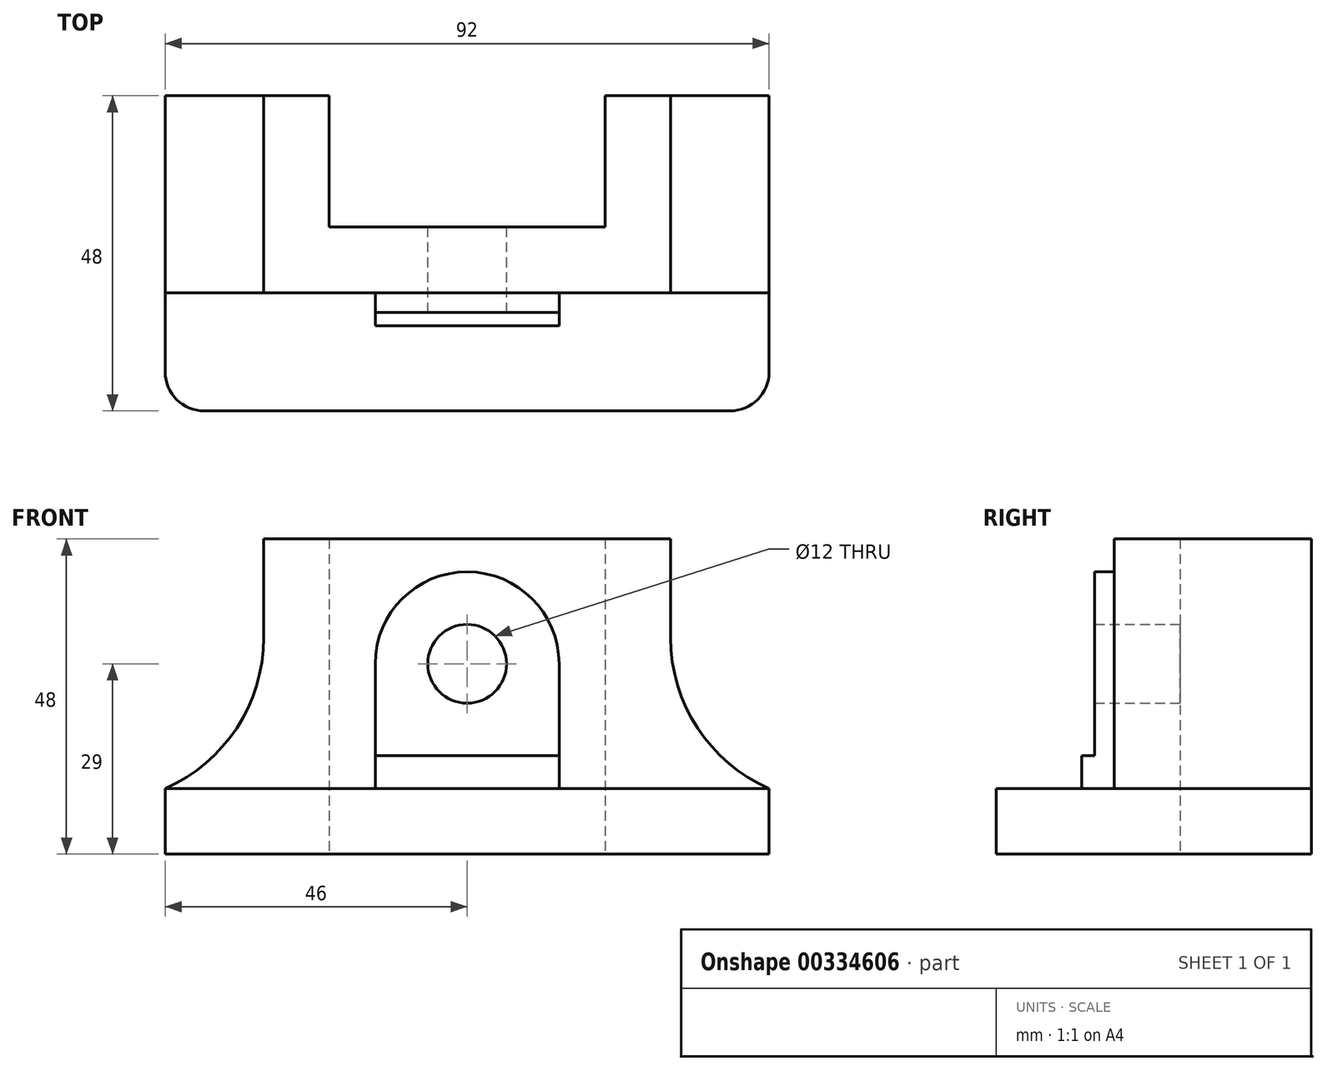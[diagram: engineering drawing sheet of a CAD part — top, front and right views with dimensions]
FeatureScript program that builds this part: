
annotation { "Feature Type Name" : "Feature", "Feature Type Description" : "" }
export const myFeature = defineFeature(function(context is Context, id is Id, definition is map)
    precondition{}
    {
        {
            var Q0;
            Q0=qCreatedBy(makeId("Top.planeOp"),FACE);
            var sketch = newSketch(context, id + "F0", { "sketchPlane" : qUnion([Q0])});
            skPoint(sketch, "E0.middle", {"position": v(0, 0) * mm});
            skLineSegment(sketch, "E1", {"start": v(0, 11.63) * mm, "end": v(-21, 11.63) * mm});
            skLineSegment(sketch, "E2", {"start": v(-21, 11.63) * mm, "end": v(-21, 31.63) * mm});
            skLineSegment(sketch, "E3", {"start": v(-21, 31.63) * mm, "end": v(-31, 31.63) * mm});
            skLineSegment(sketch, "E4", {"start": v(-31, 31.63) * mm, "end": v(-31, 1.63) * mm});
            skLineSegment(sketch, "E5", {"start": v(-31, 1.63) * mm, "end": v(0, 1.63) * mm});
            skLineSegment(sketch, "E6.MirrorCS", {"start": v(31, 31.63) * mm, "end": v(31, 1.63) * mm});
            skLineSegment(sketch, "E7.MirrorCS", {"start": v(31, 1.63) * mm, "end": v(0, 1.63) * mm});
            skLineSegment(sketch, "E8.MirrorCS", {"start": v(0, 11.63) * mm, "end": v(21, 11.63) * mm});
            skLineSegment(sketch, "E9.MirrorCS", {"start": v(21, 11.63) * mm, "end": v(21, 31.63) * mm});
            skLineSegment(sketch, "E10.MirrorCS", {"start": v(21, 31.63) * mm, "end": v(31, 31.63) * mm});
            skLineSegment(sketch, "E11", {"start": v(-46, 31.63) * mm, "end": v(-46, -16.37) * mm});
            skLineSegment(sketch, "E12", {"start": v(-46, -16.37) * mm, "end": v(0, -16.37) * mm});
            skLineSegment(sketch, "E13", {"start": v(-31, 31.63) * mm, "end": v(-46, 31.63) * mm});
            skLineSegment(sketch, "E14.MirrorCS", {"start": v(46, -16.37) * mm, "end": v(0, -16.37) * mm});
            skLineSegment(sketch, "E15.MirrorCS", {"start": v(31, 31.63) * mm, "end": v(46, 31.63) * mm});
            skLineSegment(sketch, "E16.MirrorCS", {"start": v(46, 31.63) * mm, "end": v(46, -16.37) * mm});
            skSolve(sketch);
        }
        {
            var Q0;
            Q0=makeQuery(id+"F0.imprint","IMPRINT",FACE,{"disambiguationData":[TD([[makeQuery(id+"F0.imprint","IMPRINT",EDGE,{"derivedFrom":sQuery(id+"F0.wireOp",EDGE,"E1")}),1.0]])]});
            extrude(context, id + "F1", {"entities" : qUnion([Q0]), "depth" : 48 * mm});
        }
        {
            var Q0;
            Q0 = qSketchRegion(id + "F0", true);
            extrude(context, id + "F2", {"entities" : qUnion([Q0]), "operationType" : NewBodyOperationType.ADD, "depth" : 10 * mm});
        }
        {
            var Q0;
            Q0=makeQuery(id+"F2.opExtrude","SWEPT_EDGE",EDGE,{"disambiguationData":[OSD([sQuery(id+"F0.wireOp",EDGE,"E11"),sQuery(id+"F0.wireOp",EDGE,"E12")])]});
            var Q1;
            Q1=makeQuery(id+"F2.opExtrude","SWEPT_EDGE",EDGE,{"disambiguationData":[OSD([sQuery(id+"F0.wireOp",EDGE,"E14.MirrorCS"),sQuery(id+"F0.wireOp",EDGE,"E16.MirrorCS")])]});
            fillet(context, id + "F3", {"entities" : qUnion([Q0, Q1]), "radius" : 6 * mm, "tangentPropagation" : true, "allowEdgeOverflow" : false});
        }
        {
            var Q0;
            Q0=makeQuery(id+"F2.boolean.opBoolean","INTERSECT",EDGE,{"derivedFrom":[makeQuery(id+"F1.opExtrude","SWEPT_FACE",FACE,{"disambiguationData":[OSD([sQuery(id+"F0.wireOp",EDGE,"E4")])]}),makeQuery(id+"F2.opExtrude","CAP_FACE",FACE,{"disambiguationData":[OSD([sQuery(id+"F0.wireOp",EDGE,"E1"),sQuery(id+"F0.wireOp",EDGE,"E2"),sQuery(id+"F0.wireOp",EDGE,"E3"),sQuery(id+"F0.wireOp",EDGE,"E8.MirrorCS"),sQuery(id+"F0.wireOp",EDGE,"E9.MirrorCS"),sQuery(id+"F0.wireOp",EDGE,"E10.MirrorCS"),sQuery(id+"F0.wireOp",EDGE,"E11"),sQuery(id+"F0.wireOp",EDGE,"E12"),sQuery(id+"F0.wireOp",EDGE,"E13"),sQuery(id+"F0.wireOp",EDGE,"E14.MirrorCS"),sQuery(id+"F0.wireOp",EDGE,"E15.MirrorCS"),sQuery(id+"F0.wireOp",EDGE,"E16.MirrorCS")])],"isStart":false})]});
            fillet(context, id + "F4", {"entities" : qUnion([Q0]), "radius" : 25 * mm, "tangentPropagation" : true, "allowEdgeOverflow" : false});
        }
        {
            var Q0;
            Q0=makeQuery(id+"F2.boolean.opBoolean","INTERSECT",EDGE,{"derivedFrom":[makeQuery(id+"F1.opExtrude","SWEPT_FACE",FACE,{"disambiguationData":[OSD([sQuery(id+"F0.wireOp",EDGE,"E6.MirrorCS")])]}),makeQuery(id+"F2.opExtrude","CAP_FACE",FACE,{"disambiguationData":[OSD([sQuery(id+"F0.wireOp",EDGE,"E1"),sQuery(id+"F0.wireOp",EDGE,"E2"),sQuery(id+"F0.wireOp",EDGE,"E3"),sQuery(id+"F0.wireOp",EDGE,"E8.MirrorCS"),sQuery(id+"F0.wireOp",EDGE,"E9.MirrorCS"),sQuery(id+"F0.wireOp",EDGE,"E10.MirrorCS"),sQuery(id+"F0.wireOp",EDGE,"E11"),sQuery(id+"F0.wireOp",EDGE,"E12"),sQuery(id+"F0.wireOp",EDGE,"E13"),sQuery(id+"F0.wireOp",EDGE,"E14.MirrorCS"),sQuery(id+"F0.wireOp",EDGE,"E15.MirrorCS"),sQuery(id+"F0.wireOp",EDGE,"E16.MirrorCS")])],"isStart":false})]});
            fillet(context, id + "F5", {"entities" : qUnion([Q0]), "radius" : 25 * mm, "tangentPropagation" : true, "allowEdgeOverflow" : false});
        }
        {
            var Q0;
            Q0=makeQuery(id+"F1.opExtrude","SWEPT_FACE",FACE,{"disambiguationData":[OSD([sQuery(id+"F0.wireOp",EDGE,"E5"),sQuery(id+"F0.wireOp",EDGE,"E7.MirrorCS")])]});
            var sketch = newSketch(context, id + "F6", { "sketchPlane" : qUnion([Q0])});
            skCircle(sketch, "E17", {"center": v(0, 29) * mm, "radius": 14 * mm});
            skCircle(sketch, "E18", {"center": v(0, 29) * mm, "radius": 6 * mm});
            skLineSegment(sketch, "E19", {"start": v(-14, 29) * mm, "end": v(-14, 10) * mm});
            skLineSegment(sketch, "E20", {"start": v(14, 29) * mm, "end": v(14, 10) * mm});
            skLineSegment(sketch, "E21", {"start": v(-14, 10) * mm, "end": v(14, 10) * mm});
            skLineSegment(sketch, "E22", {"start": v(-14, 15) * mm, "end": v(14, 15) * mm});
            skSolve(sketch);
        }
        {
            var Q0;
            {var subQ4=sQuery(id+"F6.wireOp",EDGE,"E21");Q0=makeQuery(id+"F6.imprint","IMPRINT",FACE,{"disambiguationData":[TD([[makeQuery(id+"F6.imprint","IMPRINT",EDGE,{"derivedFrom":subQ4}),1.0]])]});}
            extrude(context, id + "F7", {"entities" : qUnion([Q0]), "operationType" : NewBodyOperationType.ADD, "depth" : 5 * mm});
        }
        {
            var Q0;
            Q0 = qSketchRegion(id + "F6", true);
            extrude(context, id + "F8", {"entities" : qUnion([Q0]), "operationType" : NewBodyOperationType.ADD, "depth" : 3 * mm});
        }
        {
            var Q0;
            Q0=makeQuery(id+"F8.boolean.opBoolean","SPLIT",FACE,{"disambiguationData":[TD([makeQuery(id+"F8.opExtrude","SWEPT_FACE",FACE,{"disambiguationData":[OSD([sQuery(id+"F6.wireOp",EDGE,"E18")])]})])],"derivedFrom":makeQuery(id+"F1.opExtrude","SWEPT_FACE",FACE,{"disambiguationData":[OSD([sQuery(id+"F0.wireOp",EDGE,"E5"),sQuery(id+"F0.wireOp",EDGE,"E7.MirrorCS")])]})});
            extrude(context, id + "F9", {"entities" : qUnion([Q0]), "operationType" : NewBodyOperationType.REMOVE, "oppositeDirection" : true, "depth" : 25 * mm});
        }
    });
